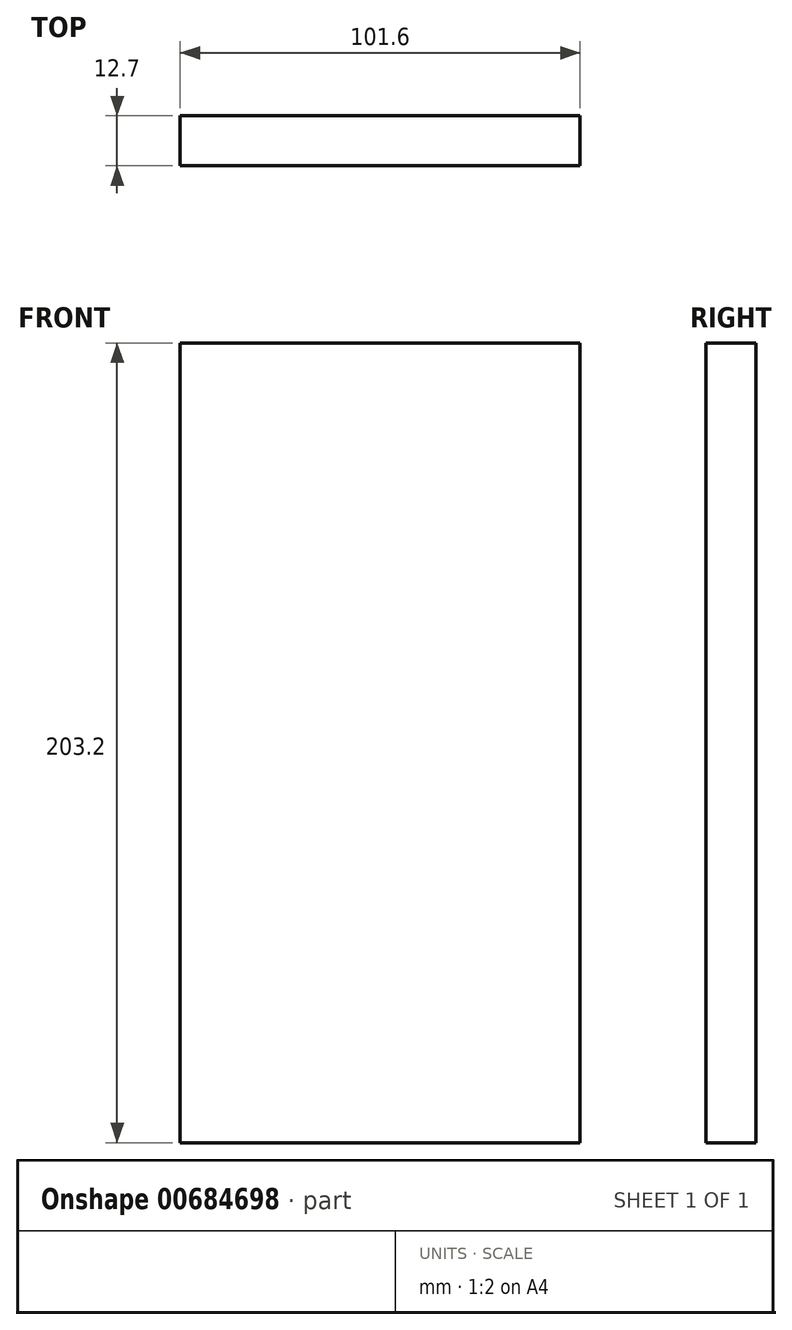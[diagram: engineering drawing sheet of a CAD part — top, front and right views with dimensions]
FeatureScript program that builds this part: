
annotation { "Feature Type Name" : "Feature", "Feature Type Description" : "" }
export const myFeature = defineFeature(function(context is Context, id is Id, definition is map)
    precondition{}
    {
        {
            var Q0;
            Q0=qCreatedBy(makeId("Front.planeOp"),FACE);
            var sketch = newSketch(context, id + "F0", { "sketchPlane" : qUnion([Q0])});
            skLineSegment(sketch, "E0.bottom", {"start": v(-57.4, 148.3) * mm, "end": v(44.2, 148.3) * mm});
            skLineSegment(sketch, "E0.top", {"start": v(-57.4, -54.9) * mm, "end": v(44.2, -54.9) * mm});
            skLineSegment(sketch, "E0.left", {"start": v(-57.4, 148.3) * mm, "end": v(-57.4, -54.9) * mm});
            skLineSegment(sketch, "E0.right", {"start": v(44.2, 148.3) * mm, "end": v(44.2, -54.9) * mm});
            skSolve(sketch);
        }
        {
            var Q0;
            Q0=qSketchRegion(id+"F0",true);
            extrude(context, id + "F1", {"entities" : qUnion([Q0]), "depth" : 12.7 * mm, "offsetDistance" : 25.4 * mm});
        }
    });
